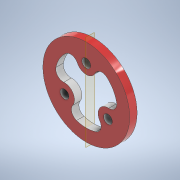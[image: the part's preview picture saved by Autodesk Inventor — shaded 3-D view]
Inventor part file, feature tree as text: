
AUTODESK INVENTOR PART (.ipt)
format: ipt  version: 2021 (Build 250183000, 183)  size: 148,480 bytes
history: native  units: mm
features: other x3, plane x1, extrude x1, sketch x1, reference x1
ambient origin geometry x8: Origin, YZ Plane, XZ Plane, XY Plane, X Axis, Y Axis, Z Axis, Center Point
bodies: Solid1 (feature_tree)
feature tree (7):
  plane  "Work Plane1"
  extrude  "Extrusion1"  Depth=3.0mm
  sketch  "Sketch1"  dims[d0=3.0mm d1=0.0mm d2=3.5mm d3=3.5mm d4=3.5mm]
  reference  "Reference1"
  other  "Z:\softHandProsthesis.iam"
  other  "softHandProsthesis.iam"
  other  "palm_connector:1"
